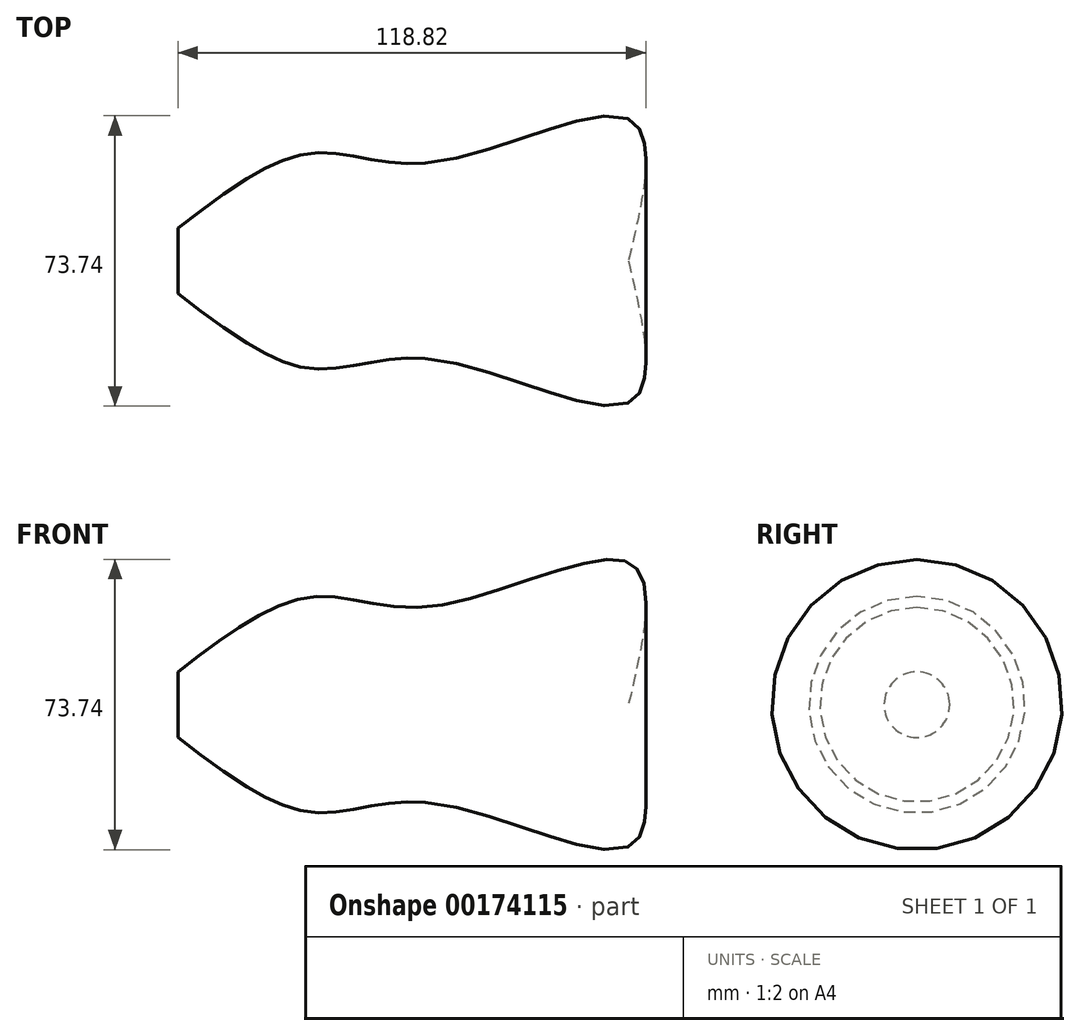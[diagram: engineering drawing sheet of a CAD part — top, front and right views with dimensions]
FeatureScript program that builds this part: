
annotation { "Feature Type Name" : "Feature", "Feature Type Description" : "" }
export const myFeature = defineFeature(function(context is Context, id is Id, definition is map)
    precondition{}
    {
        {
            var Q0;
            Q0=qCreatedBy(makeId("Front.planeOp"),FACE);
            var sketch = newSketch(context, id + "F0", { "sketchPlane" : qUnion([Q0])});
            skLineSegment(sketch, "E0", {"start": v(-43.03, 8.35) * mm, "end": v(-43.03, 0) * mm});
            skFitSpline(sketch, "E1", {"points": [v(-43.03, 8.35) * mm, v(-9.5, 27.34) * mm, v(21.87, 25.04) * mm, v(71.66, 35.98) * mm, v(71.38, 0) * mm], "startDerivative": vector(138.89, 107.07) * mm, "endDerivative": vector(-47.13, -201.37) * mm});
            skLineSegment(sketch, "E2", {"start": v(-43.03, 0) * mm, "end": v(71.38, 0) * mm});
            skSolve(sketch);
        }
        {
            var Q0;
            Q0 = qSketchRegion(id + "F0", true);
            var Q1;
            Q1=sQuery(id+"F0.wireOp",EDGE,"E2");
            revolve(context, id + "F1", {"entities" : qUnion([Q0]), "axis" : qUnion([Q1]), "revolveType" : RevolveType.FULL});
        }
    });
